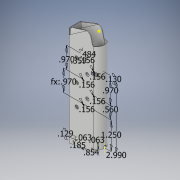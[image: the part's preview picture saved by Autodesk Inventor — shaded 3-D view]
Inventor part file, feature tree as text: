
AUTODESK INVENTOR PART (.ipt)
format: ipt  version: 2018.3 (Build 223284000, 284)  size: 390,144 bytes
history: native  units: in
note: dims shown in document units (in); Inventor stores cm internally (conversion verified against a paired STEP export)
features: sketch x9, extrude x7, plane x4, split x3, other x2, boolean_combine x1
ambient origin geometry x8: Origin, YZ Plane, XZ Plane, XY Plane, X Axis, Y Axis, Z Axis, Center Point
bodies: Solid1 (feature_tree), Solid2 (feature_tree), Solid3 (feature_tree), Solid4 (feature_tree), Solid5 (feature_tree), Solid6 (feature_tree), Solid7 (feature_tree)
feature tree (26):
  sketch  "Sketch1"  dims[d0=0.541in d1=0.2445in]
  extrude  "Extrusion1"  Depth=0.2445in
  sketch  "Sketch3"  dims[d2=0.026in d3=0.026in]
  sketch  "Sketch4"  dims[d4=0.026in d5=0.015in]
  extrude  "Extrusion2"  Depth=0.026in
  plane  "Work Plane1"
  extrude  "Extrusion3"  Depth=0.026in
  extrude  "Extrusion4"  Depth=0.81in
  plane  "Work Plane2"
  extrude  "Extrusion5"  Depth=0.8in
  sketch  "Sketch8"  dims[d11=0.4in d12=0.0618in]
  split  "Split1"
  split  "Split2"
  split  "Split3"
  plane  "Work Plane4"
  other  "Bend Part1"
  plane  "Work Plane5"
  other  "Bend Part2"
  boolean_combine  "Combine1"
  sketch  "Sketch12"  dims[d16=1.372in d17=4.4761in d18=0.3439in d19=3.0in d20=0.0in d23=0.125in d24=0.0in d25=4.005in d26=105.0deg d27=1.0994in d28=0.05in d29=1.0in d30=0.0in d31=2.0in d32=0.0in d33=0.0in d35=0.0in d36=0.5in d37=0.5497in d38=0.0in d39=0.5in d40=0.5497in d41=0.156in d42=1.25in d43=0.156in d44=0.156in d45=0.156in d46=0.156in d47=0.56in d48=0.97in d49=0.484in d50=0.359in d51=0.97in d52=0.97in d53=0.13in d54=2.99in d55=1.0in d56=0.0in d57=0.185in d58=0.854in d59=0.129in d60=0.063in d61=0.063in d62=1.0in d63=0.0in]
  extrude  "Extrusion6"  Depth=0.0618in
  extrude  "Extrusion7"  Depth=1.172in
  sketch  "Sketch5"  dims[d6=4.82in d7=0.0in d8=0.81in]
  sketch  "Sketch6"  dims[d9=0.9in d10=0.8in]
  sketch  "Sketch10"  dims[d13=0.125in d14=1.172in]
  sketch  "Sketch11"  dims[d15=1.372in]
